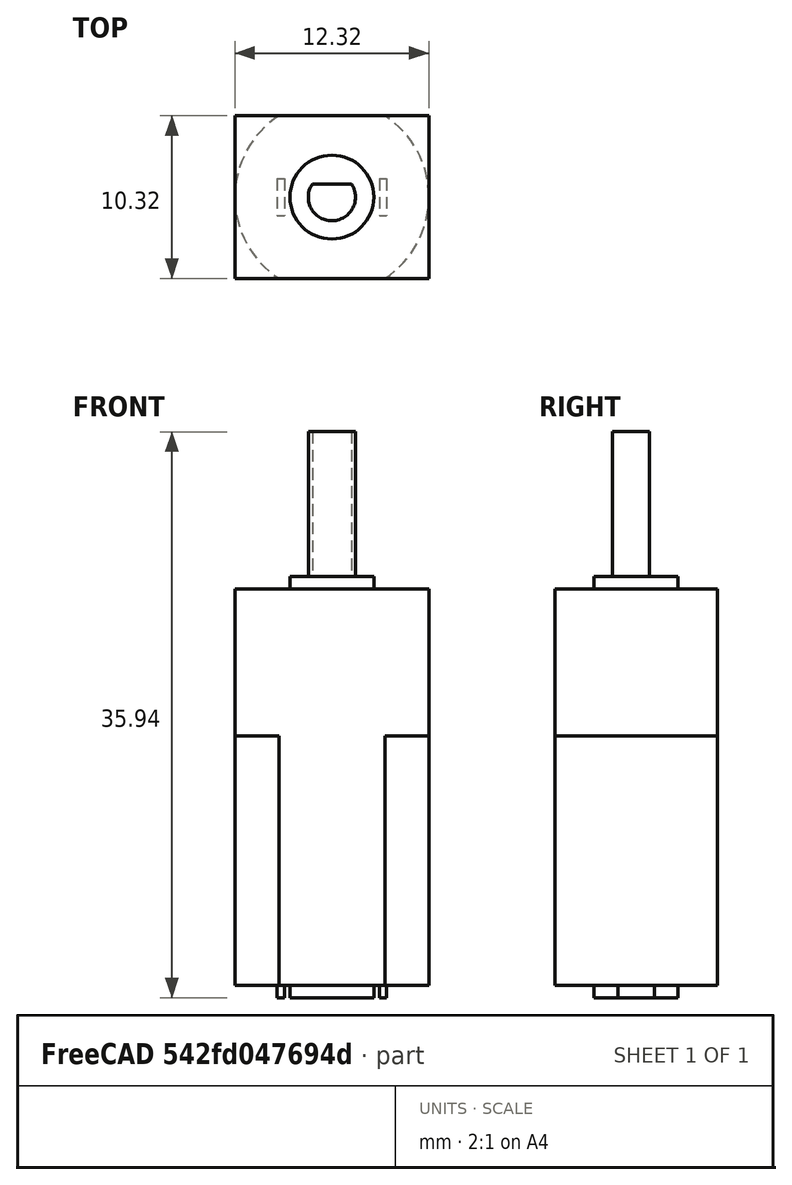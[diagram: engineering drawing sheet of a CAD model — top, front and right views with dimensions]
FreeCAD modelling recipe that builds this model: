
FCSTD DOCUMENT  (FreeCAD 1.0R1.0.1)
Label: N20_Gearbox
License: All rights reserved
LicenseURL: http://en.wikipedia.org/wiki/All_rights_reserved
objects: Part::Box×5, Part::Cylinder×3, Part::MultiFuse×3, Spreadsheet::Sheet×1, Part::MultiCommon×1, Part::Cut×1
note: 13 computed .brp shape members not serialized (recipe doc carries the construction recipe); baked Part::Feature solids carry a one-line shape summary decoded from their .brp

FEATURE [Part::Box] Box  label="Cube"
  AttacherType = Attacher::AttachEngine3D
  Height = 15.825
  Length = 12.325
  Placement = pos=(-6.1625,-5.1625,0) rot=(0,0,1;0rad)
  Width = 10.325
  expr: .Placement.Base.x = -6 - <<N20Cfg>>.outline_extend / 2
  expr: .Placement.Base.y = -5 - <<N20Cfg>>.outline_extend / 2
  expr: Height = 15.5 + <<N20Cfg>>.outline_extend
  expr: Length = 12 + <<N20Cfg>>.outline_extend
  expr: Width = 10 + <<N20Cfg>>.outline_extend
FEATURE [Part::Cylinder] Cylinder
  Angle = 360
  AttacherType = Attacher::AttachEngine3D
  FirstAngle = 0
  Height = 15.825
  Radius = 6.1625
  SecondAngle = 0
  expr: Height = 15.5 + <<N20Cfg>>.outline_extend
  expr: Radius = (12 + <<N20Cfg>>.outline_extend) / 2
FEATURE [Spreadsheet::Sheet] Spreadsheet  label="N20Cfg"
  cells = A2='Extend outline; B2(outline_extend)=0.325; C2='Used when utilizing as pressfit - this is the tolerance (in all directions) applied to the part; D2='Pressfit: 0.325; E2='Insert that requires different fixture: 0.4; A3='Shaft tolerance; B3(shaft_tolerance)=0
FEATURE [Part::MultiCommon] Common
  Shapes = -> [Box,Cylinder]
FEATURE [Part::Cylinder] Cylinder001
  Angle = 360
  AttacherType = Attacher::AttachEngine3D
  FirstAngle = 0
  Height = 26.75
  Placement = pos=(0,0,-10.125) rot=(0,0,1;0rad)
  Radius = 2.6625
  SecondAngle = 0
  expr: .Placement.Base.z = -(<<N20Cfg>>.outline_extend + 0.8 + 9)
  expr: Height = 15.5 + 2 * <<N20Cfg>>.outline_extend + 0.8 + 0.8 + 9
  expr: Radius = (5 + <<N20Cfg>>.outline_extend) / 2
FEATURE [Part::Box] Box002  label="Gearbox"
  AttacherType = Attacher::AttachEngine3D
  Height = 9.325
  Length = 12.325
  Placement = pos=(-6.1625,-5.1625,-9.325) rot=(0,0,1;0rad)
  Width = 10.325
  expr: .Placement.Base.x = -6 - <<N20Cfg>>.outline_extend / 2
  expr: .Placement.Base.y = -5 - <<N20Cfg>>.outline_extend / 2
  expr: .Placement.Base.z = -(9 + <<N20Cfg>>.outline_extend)
  expr: Height = 9 + <<N20Cfg>>.outline_extend
  expr: Length = 12 + <<N20Cfg>>.outline_extend
  expr: Width = 10 + <<N20Cfg>>.outline_extend
FEATURE [Part::Cylinder] Cylinder002
  Angle = 360
  AttacherType = Attacher::AttachEngine3D
  FirstAngle = 0
  Height = 19.325
  Radius = 1.5
  SecondAngle = 0
  expr: Height = <<N20Cfg>>.outline_extend + 10 + 9
  expr: Radius = (3 + <<N20Cfg>>.shaft_tolerance) / 2
FEATURE [Part::MultiFuse] Fusion
  Placement = pos=(0,0,0) rot=(1,0,0;3.14159rad)
  Shapes = -> [Box002,Cylinder001,Common]
FEATURE [Part::Box] Box003  label="Cube003"
  AttacherType = Attacher::AttachEngine3D
  Height = 19.325
  Length = 3.325
  Placement = pos=(-1.6625,0.8375,0) rot=(0,0,1;0rad)
  Width = 3.325
  expr: .Placement.Base.x = -(3 + <<N20Cfg>>.outline_extend) / 2
  expr: .Placement.Base.y = 2.5 - (3 + <<N20Cfg>>.outline_extend) / 2
  expr: Height = <<N20Cfg>>.outline_extend + 10 + 9
  expr: Length = 3 + <<N20Cfg>>.outline_extend
  expr: Width = 3 + <<N20Cfg>>.outline_extend
FEATURE [Part::Cut] Cut  label="Shaft"
  Base = -> Cylinder002
  Tool = -> Box003
FEATURE [Part::Box] Box004  label="Cube004"
  AttacherType = Attacher::AttachEngine3D
  Height = 16.625
  Length = 0.455
  Placement = pos=(3.0225,-1.1625,-16.625) rot=(0,0,1;0rad)
  Width = 2.325
  expr: .Placement.Base.x = -(0.13 + <<N20Cfg>>.outline_extend) / 2 + 6.5 / 2
  expr: .Placement.Base.y = -(2 + <<N20Cfg>>.outline_extend) / 2
  expr: .Placement.Base.z = -(15.5 + 0.8 + <<N20Cfg>>.outline_extend)
  expr: Height = 15.5 + 0.8 + <<N20Cfg>>.outline_extend
  expr: Length = 0.13 + <<N20Cfg>>.outline_extend
  expr: Width = 2 + <<N20Cfg>>.outline_extend
FEATURE [Part::Box] Box005  label="Cube005"
  AttacherType = Attacher::AttachEngine3D
  Height = 16.625
  Length = 0.455
  Placement = pos=(-3.4775,-1.1625,-16.625) rot=(0,0,1;0rad)
  Width = 2.325
  expr: .Placement.Base.x = -(0.13 + <<N20Cfg>>.outline_extend) / 2 - 6.5 / 2
  expr: .Placement.Base.y = -(2 + <<N20Cfg>>.outline_extend) / 2
  expr: .Placement.Base.z = -(15.5 + 0.8 + <<N20Cfg>>.outline_extend)
  expr: Height = 15.5 + 0.8 + <<N20Cfg>>.outline_extend
  expr: Length = 0.13 + <<N20Cfg>>.outline_extend
  expr: Width = 2 + <<N20Cfg>>.outline_extend
FEATURE [Part::MultiFuse] Fusion001  label="Contacts"
  Shapes = -> [Box004,Box005]
FEATURE [Part::MultiFuse] Fusion002  label="N20GearedMotor"
  Shapes = -> [Fusion,Cut,Fusion001]
